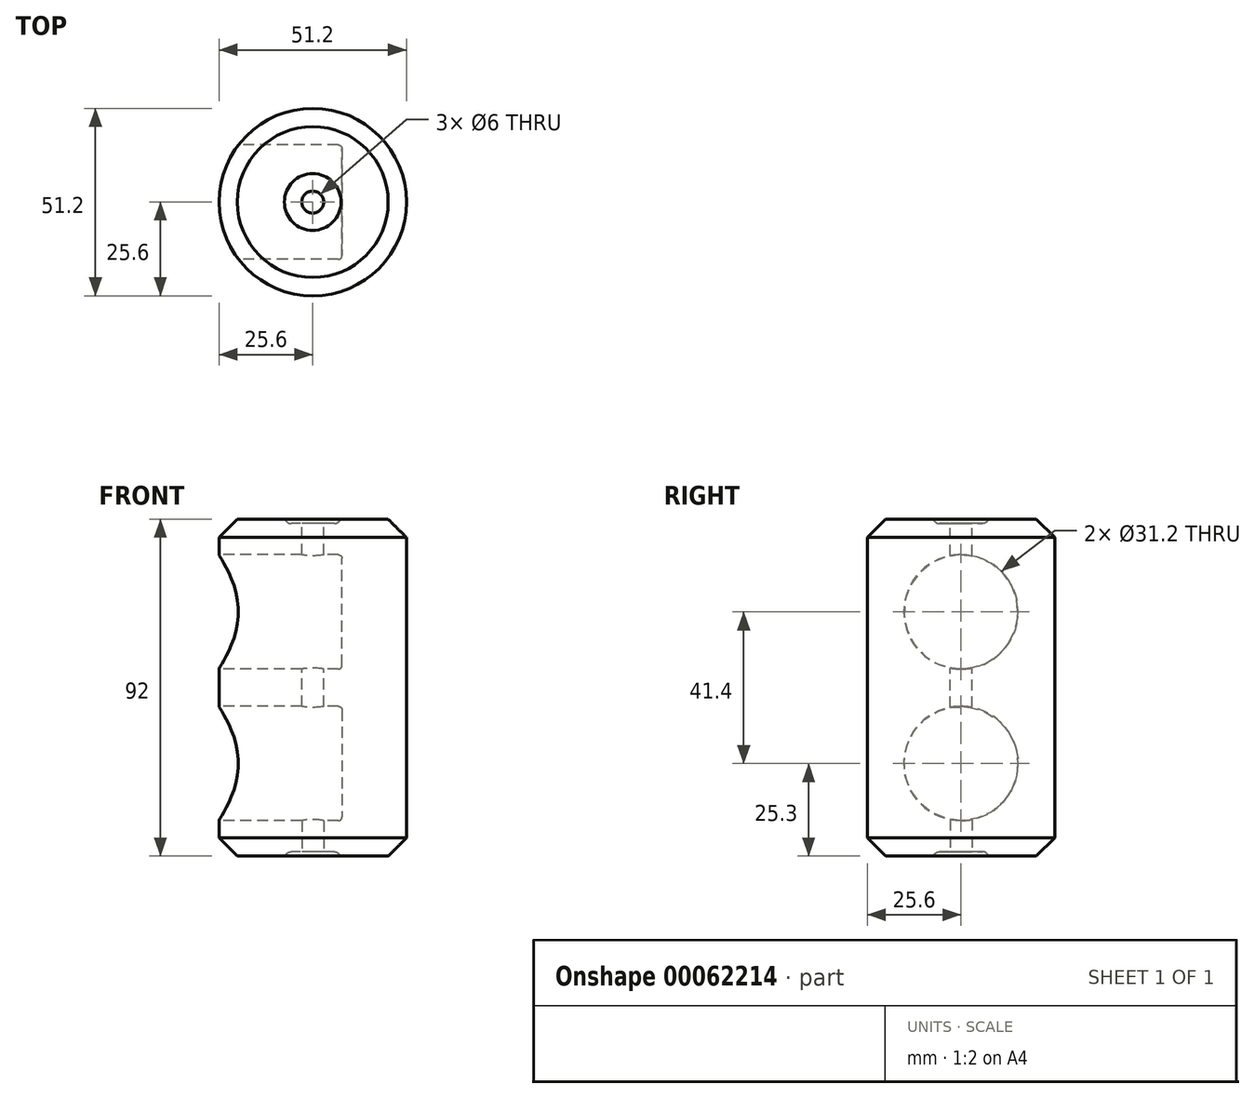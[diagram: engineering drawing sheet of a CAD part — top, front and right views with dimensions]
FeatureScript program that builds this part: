
annotation { "Feature Type Name" : "Feature", "Feature Type Description" : "" }
export const myFeature = defineFeature(function(context is Context, id is Id, definition is map)
    precondition{}
    {
        {
            var Q0;
            Q0=qCreatedBy(makeId("Front.planeOp"),FACE);
            var sketch = newSketch(context, id + "F0", { "sketchPlane" : qUnion([Q0])});
            skLineSegment(sketch, "E0.bottom", {"start": v(3, 0) * mm, "end": v(25.6, 0) * mm});
            skLineSegment(sketch, "E0.top", {"start": v(7.75, 46) * mm, "end": v(20.6, 46) * mm});
            skLineSegment(sketch, "E0.right", {"start": v(25.6, 0) * mm, "end": v(25.6, 41) * mm});
            skLineSegment(sketch, "E1", {"start": v(20.6, 46) * mm, "end": v(25.6, 41) * mm});
            skLineSegment(sketch, "E2", {"start": v(23.1, 43.5) * mm, "end": v(25.6, 46) * mm, "construction": true});
            skLineSegment(sketch, "E3", {"start": v(0, 0) * mm, "end": v(0, -12.36) * mm, "construction": true});
            skLineSegment(sketch, "E4", {"start": v(25.6, 0) * mm, "end": v(37.42, 0) * mm, "construction": true});
            skLineSegment(sketch, "E5", {"start": v(3, 44.8) * mm, "end": v(3, 0) * mm});
            skLineSegment(sketch, "E6", {"start": v(3, 44.8) * mm, "end": v(5.93, 44.8) * mm});
            skLineSegment(sketch, "E7", {"start": v(6.99, 45.24) * mm, "end": v(7.75, 46) * mm});
            skPoint(sketch, "E8.orphan", {"position": v(3, 46) * mm});
            skPoint(sketch, "E9.visualSharp", {"position": v(6.55, 44.8) * mm});
            skArc(sketch, "E9.filletArc", {"start": v(5.93, 44.8) * mm, "mid": v(6.5, 44.91) * mm, "end": v(6.99, 45.24) * mm});
            skSolve(sketch);
        }
        {
            var Q0;
            Q0=qSketchRegion(id+"F0",true);
            var Q1;
            Q1=sQuery(id+"F0.wireOp",EDGE,"E3");
            revolve(context, id + "F1", {"entities" : qUnion([Q0]), "axis" : qUnion([Q1]), "revolveType" : RevolveType.FULL});
        }
        {
            var Q0;
            Q0=qCreatedBy(makeId("Front.planeOp"),FACE);
            var sketch = newSketch(context, id + "F2", { "sketchPlane" : qUnion([Q0])});
            skLineSegment(sketch, "E10.bottom", {"start": v(-25.6, 36.3) * mm, "end": v(8, 36.3) * mm});
            skLineSegment(sketch, "E10.top", {"start": v(-25.6, 20.7) * mm, "end": v(8, 20.7) * mm});
            skLineSegment(sketch, "E10.right", {"start": v(8, 36.3) * mm, "end": v(8, 20.7) * mm});
            skLineSegment(sketch, "E11", {"start": v(-25.6, 20.7) * mm, "end": v(-43.54, 20.7) * mm, "construction": true});
            skLineSegment(sketch, "E12", {"start": v(-25.6, 20.7) * mm, "end": v(-25.6, 36.3) * mm});
            skLineSegment(sketch, "E13", {"start": v(-25.66, 0) * mm, "end": v(-55.12, 0) * mm, "construction": true});
            skSolve(sketch);
        }
        {
            var Q0;
            Q0=qSketchRegion(id+"F2",true);
            var Q1;
            Q1=sQuery(id+"F2.wireOp",EDGE,"E11");
            revolve(context, id + "F3", {"operationType" : NewBodyOperationType.REMOVE, "entities" : qUnion([Q0]), "axis" : qUnion([Q1]), "revolveType" : RevolveType.FULL, "oppositeDirection" : true});
        }
        {
            var Q0;
            Q0=makeQuery(id+"F3.boolean.opBoolean","COPY",EDGE,{"derivedFrom":makeQuery(id+"F3.opRevolve","SWEPT_EDGE",EDGE,{"disambiguationData":[OSD([sQuery(id+"F2.wireOp",EDGE,"E10.bottom"),sQuery(id+"F2.wireOp",EDGE,"E10.right")])]})});
            fillet(context, id + "F4", {"entities" : qUnion([Q0]), "radius" : 1 * mm, "tangentPropagation" : true, "allowEdgeOverflow" : false});
        }
        {
            var Q0;
            Q0=makeQuery(id+"F1.opRevolve","SWEPT_BODY",BODY,{"disambiguationData":[OSD([sQuery(id+"F0.wireOp",EDGE,"E0.bottom"),sQuery(id+"F0.wireOp",EDGE,"E0.top"),sQuery(id+"F0.wireOp",EDGE,"E0.right"),sQuery(id+"F0.wireOp",EDGE,"E1"),sQuery(id+"F0.wireOp",EDGE,"E5")])]});
            var Q1;
            Q1=qCreatedBy(makeId("Top.planeOp"),FACE);
            mirror(context, id + "F5", {"operationType" : NewBodyOperationType.ADD, "entities" : qUnion([Q0]), "mirrorPlane" : qUnion([Q1])});
        }
    });
